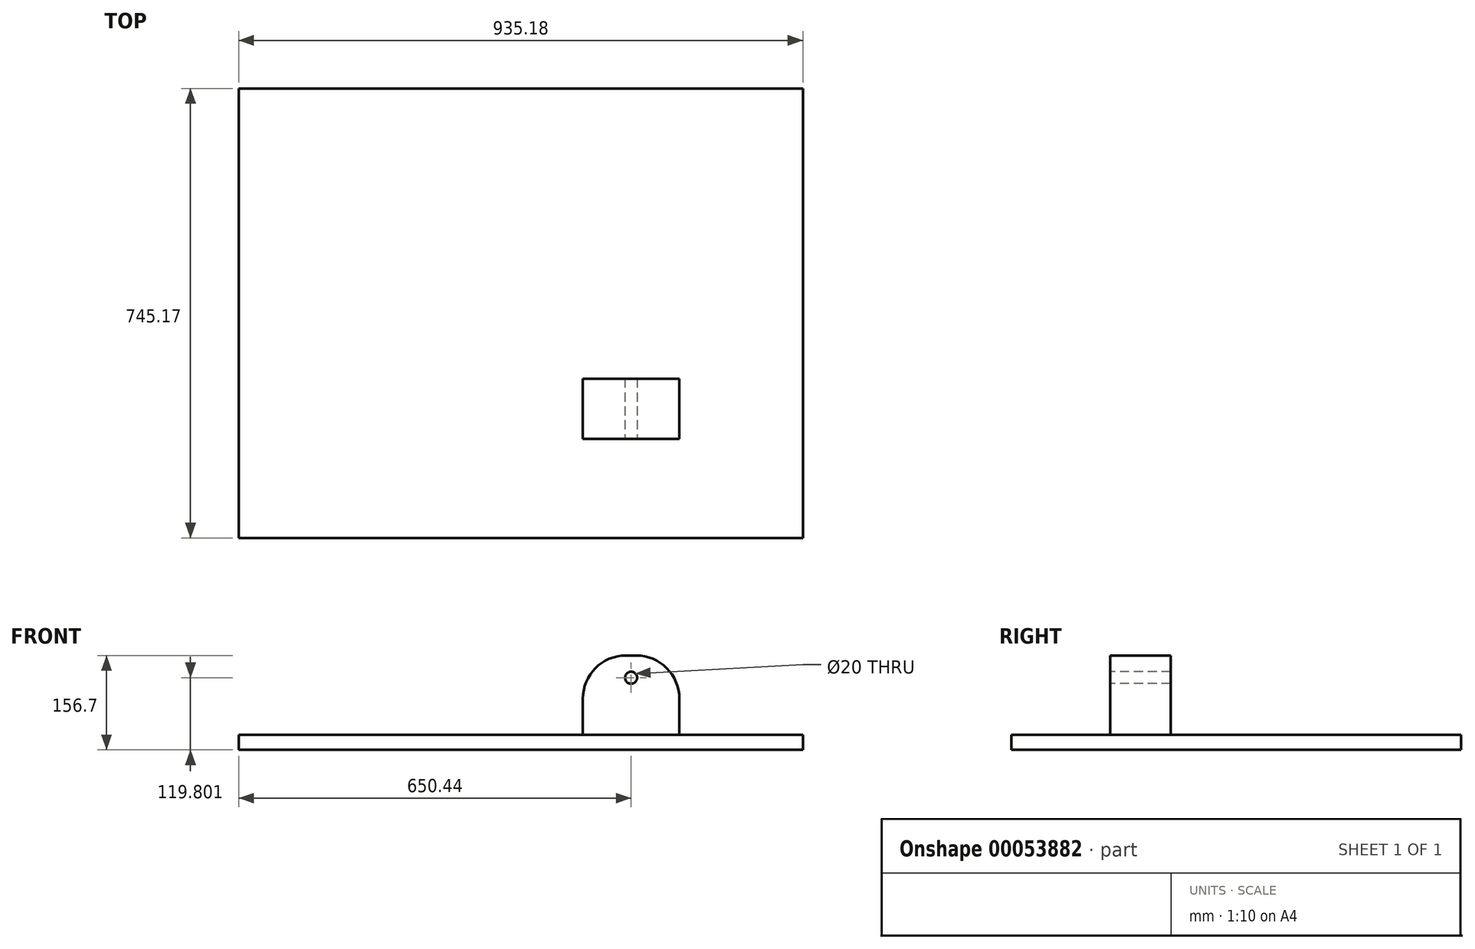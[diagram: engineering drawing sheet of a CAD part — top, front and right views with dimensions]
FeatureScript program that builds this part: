
annotation { "Feature Type Name" : "Feature", "Feature Type Description" : "" }
export const myFeature = defineFeature(function(context is Context, id is Id, definition is map)
    precondition{}
    {
        {
            var Q0;
            Q0=qCreatedBy(makeId("Top.planeOp"),FACE);
            var sketch = newSketch(context, id + "F0", { "sketchPlane" : qUnion([Q0])});
            skLineSegment(sketch, "E0.bottom", {"start": v(-730.44, 286) * mm, "end": v(204.74, 286) * mm});
            skLineSegment(sketch, "E0.top", {"start": v(-730.44, -459.17) * mm, "end": v(204.74, -459.17) * mm});
            skLineSegment(sketch, "E0.left", {"start": v(-730.44, 286) * mm, "end": v(-730.44, -459.17) * mm});
            skLineSegment(sketch, "E0.right", {"start": v(204.74, 286) * mm, "end": v(204.74, -459.17) * mm});
            skSolve(sketch);
        }
        {
            var Q0;
            Q0=makeQuery(id+"F0.imprint","IMPRINT",FACE,{"disambiguationData":[TD([[makeQuery(id+"F0.imprint","IMPRINT",EDGE,{"derivedFrom":sQuery(id+"F0.wireOp",EDGE,"E0.bottom")}),-1.0]])]});
            extrude(context, id + "F1", {"entities" : qUnion([Q0]), "depth" : 25 * mm});
        }
        {
            var Q0;
            Q0=makeQuery(id+"F1.opExtrude","CAP_FACE",FACE,{"disambiguationData":[OSD([sQuery(id+"F0.wireOp",EDGE,"E0.bottom"),sQuery(id+"F0.wireOp",EDGE,"E0.top"),sQuery(id+"F0.wireOp",EDGE,"E0.left"),sQuery(id+"F0.wireOp",EDGE,"E0.right")])],"isStart":false});
            var sketch = newSketch(context, id + "F2", { "sketchPlane" : qUnion([Q0])});
            skLineSegment(sketch, "E1.bottom", {"start": v(-160, -295.17) * mm, "end": v(0, -295.17) * mm});
            skLineSegment(sketch, "E1.top", {"start": v(-160, -195.17) * mm, "end": v(0, -195.17) * mm});
            skLineSegment(sketch, "E1.left", {"start": v(-160, -295.17) * mm, "end": v(-160, -195.17) * mm});
            skLineSegment(sketch, "E1.right", {"start": v(0, -295.17) * mm, "end": v(0, -195.17) * mm});
            skSolve(sketch);
        }
        {
            var Q0;
            Q0=makeQuery(id+"F2.imprint","IMPRINT",FACE,{"disambiguationData":[TD([[makeQuery(id+"F2.imprint","IMPRINT",EDGE,{"derivedFrom":sQuery(id+"F2.wireOp",EDGE,"E1.bottom")}),1.0]])]});
            extrude(context, id + "F3", {"entities" : qUnion([Q0]), "operationType" : NewBodyOperationType.ADD, "depth" : 131.7 * mm});
        }
        {
            var Q0;
            Q0=makeQuery(id+"F3.opExtrude","SWEPT_FACE",FACE,{"disambiguationData":[OSD([sQuery(id+"F2.wireOp",EDGE,"E1.bottom")])]});
            var sketch = newSketch(context, id + "F4", { "sketchPlane" : qUnion([Q0])});
            skCircle(sketch, "E2", {"center": v(-80, 119.8) * mm, "radius": 26.1 * mm});
            skSolve(sketch);
        }
        {
            var Q0;
            Q0=sQuery(id+"F4.wireOp",VERTEX,"E2.center");
            var Q1;
            Q1=makeQuery(id+"F1.opExtrude","SWEPT_BODY",BODY,{"disambiguationData":[OSD([sQuery(id+"F0.wireOp",EDGE,"E0.bottom"),sQuery(id+"F0.wireOp",EDGE,"E0.top"),sQuery(id+"F0.wireOp",EDGE,"E0.left"),sQuery(id+"F0.wireOp",EDGE,"E0.right")])]});
            hole(context, id + "F5", {"style" : HoleStyle.SIMPLE, "holeDiameter" : 20 * mm, "endStyle" : HoleEndStyle.THROUGH, "locations" : qUnion([Q0]), "scope" : qUnion([Q1])});
        }
        {
            var Q0;
            Q0=makeQuery(id+"F3.opExtrude","CAP_EDGE",EDGE,{"disambiguationData":[OSD([sQuery(id+"F2.wireOp",EDGE,"E1.right")])],"isStart":false});
            var Q1;
            Q1=makeQuery(id+"F3.opExtrude","CAP_EDGE",EDGE,{"disambiguationData":[OSD([sQuery(id+"F2.wireOp",EDGE,"E1.left")])],"isStart":false});
            fillet(context, id + "F6", {"entities" : qUnion([Q0, Q1]), "radius" : 71.84 * mm, "tangentPropagation" : true, "allowEdgeOverflow" : false});
        }
    });
